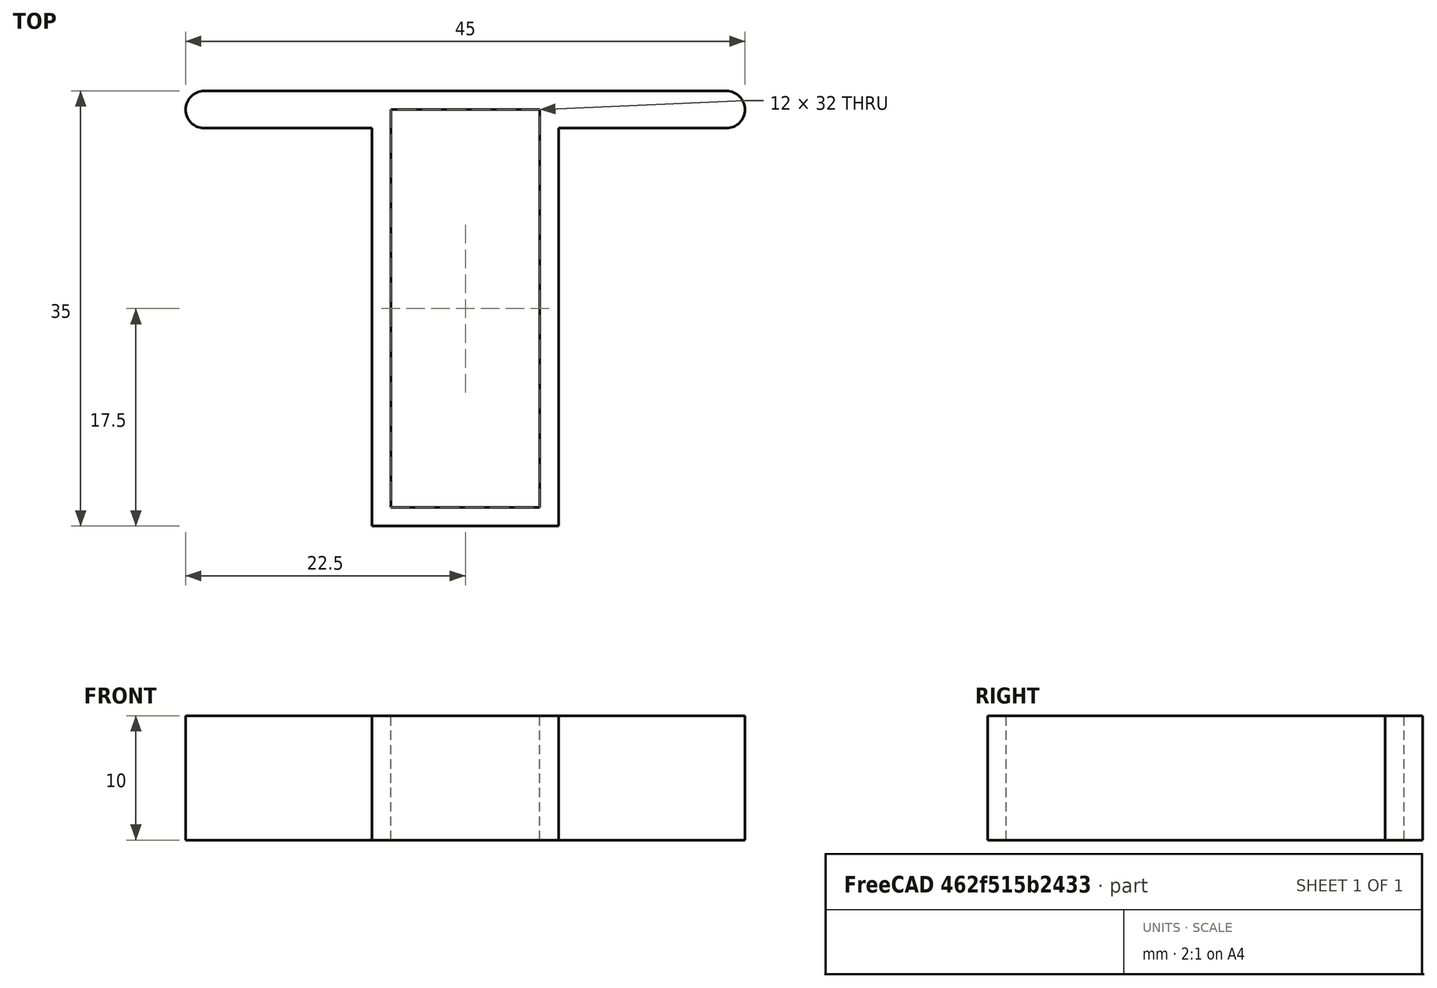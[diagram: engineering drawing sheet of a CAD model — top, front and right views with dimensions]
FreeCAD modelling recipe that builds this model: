
FCSTD DOCUMENT  (FreeCAD 0.18R16117 (Git))
Label: Perfil_R_5853
License: All rights reserved
LicenseURL: http://en.wikipedia.org/wiki/All_rights_reserved
objects: Spreadsheet::Sheet×1, Sketcher::SketchObject×1, PartDesign::Pad×1, PartDesign::Body×1
note: 4 computed .brp shape members not serialized (recipe doc carries the construction recipe); baked Part::Feature solids carry a one-line shape summary decoded from their .brp

FEATURE [Spreadsheet::Sheet] Spreadsheet  label="Tabla"
  cells = B1=Serie; C1=Serie_A; D1=Serie_B; E1=Serie_C; A2=Espesor; B2(Espesor_serie_A)=1.5; C2=1.5; D2=2; E2=2; A3=Alto; B3(Alto_serie_A)=35; C3=35; D3=50; E3=50; A4=Ancho; B4(Ancho_serie_A)=30; C4=30; D4=35; E4=60; A5=Ala; B5(Ala_serie_A)=15; C5=15; D5=15; E5=20
FEATURE [Sketcher::SketchObject] Sketch
  MapMode = 5
  Support = -> [XY_Plane]
  expr: Constraints[46] = Tabla.Ancho_serie_A + Tabla.Ala_serie_A - 2 * Tabla.Espesor_serie_A
  expr: Constraints[43] = Tabla.Alto_serie_A - Tabla.Espesor_serie_A
  expr: Constraints[45] = Tabla.Espesor_serie_A
  expr: Constraints[15] = Tabla.Ancho_serie_A - Tabla.Ala_serie_A
  expr: Constraints[42] = Tabla.Espesor_serie_A
  expr: Constraints[40] = Tabla.Espesor_serie_A
  expr: Constraints[26] = Tabla.Alto_serie_A
  expr: Constraints[38] = Tabla.Alto_serie_A - 2 * Tabla.Espesor_serie_A
  expr: Constraints[25] = Tabla.Ancho_serie_A + Tabla.Ala_serie_A
  expr: Constraints[37] = Tabla.Ancho_serie_A - Tabla.Ala_serie_A - 2 * Tabla.Espesor_serie_A
  expr: Constraints[39] = Tabla.Espesor_serie_A
  sketch-geometry (16):
    g0: LineSegment StartX=15 StartY=0 StartZ=0 EndX=15 EndY=32 EndZ=0
    g1: LineSegment StartX=15 StartY=32 StartZ=0 EndX=1.5 EndY=32 EndZ=0
    g2: LineSegment StartX=1.49999 StartY=35 StartZ=0 EndX=43.5 EndY=35 EndZ=0
    g3: LineSegment StartX=43.5 StartY=32 StartZ=0 EndX=30 EndY=32 EndZ=0
    g4: LineSegment StartX=30 StartY=32 StartZ=0 EndX=30 EndY=0 EndZ=0
    g5: LineSegment StartX=30 StartY=0 StartZ=0 EndX=15 EndY=0 EndZ=0
    g6: ArcOfCircle CenterX=43.5 CenterY=33.5 CenterZ=0 NormalX=0 NormalY=0 NormalZ=1 AngleXU=0 Radius=1.5 StartAngle=4.71239 EndAngle=7.85398
    g7: ArcOfCircle CenterX=1.5 CenterY=33.5 CenterZ=0 NormalX=0 NormalY=0 NormalZ=1 AngleXU=0 Radius=1.5 StartAngle=1.5708 EndAngle=4.71239
    g8: LineSegment [constr] StartX=0 StartY=0 StartZ=0 EndX=45 EndY=0 EndZ=0
    g9: LineSegment [constr] StartX=45 StartY=0 StartZ=0 EndX=45 EndY=35 EndZ=0
    g10: LineSegment [constr] StartX=45 StartY=35 StartZ=0 EndX=0 EndY=35 EndZ=0
    g11: LineSegment [constr] StartX=0 StartY=35 StartZ=0 EndX=0 EndY=0 EndZ=0
    g12: LineSegment StartX=16.5 StartY=33.5 StartZ=0 EndX=28.5 EndY=33.5 EndZ=0
    g13: LineSegment StartX=28.5 StartY=33.5 StartZ=0 EndX=28.5 EndY=1.5 EndZ=0
    g14: LineSegment StartX=28.5 StartY=1.5 StartZ=0 EndX=16.5 EndY=1.5 EndZ=0
    g15: LineSegment StartX=16.5 StartY=1.5 StartZ=0 EndX=16.5 EndY=33.5 EndZ=0
  constraints (47):
    c: PointOnObject(g0,g-1)
    c: Vertical(g0)
    c: Coincident(g0,g1)
    c: Horizontal(g1)
    c: Horizontal(g2)
    c: Coincident(g3,g4)
    c: PointOnObject(g4,g-1)
    c: Vertical(g4)
    c: Coincident(g4,g5)
    c: Coincident(g5,g0)
    c: Equal(g3,g1)
    c: Horizontal(g3)
    c: Coincident(g6,g2)
    c: Equal(g6,g7)
    c: Coincident(g7,g2)
    c: DistanceX(g5,g5) = 15
    c: Coincident(g8,g9)
    c: Coincident(g9,g10)
    c: Coincident(g10,g11)
    c: Coincident(g11,g8)
    c: Horizontal(g8)
    c: Horizontal(g10)
    c: Vertical(g9)
    c: Vertical(g11)
    c: Coincident(g8,g-1)
    c: DistanceX(g10,g10) = 45
    c: DistanceY(g9,g9) = 35
    c: Equal(g0,g4)
    c: PointOnObject(g2,g10)
    c: Coincident(g12,g13)
    c: Coincident(g13,g14)
    c: Coincident(g14,g15)
    c: Coincident(g15,g12)
    c: Horizontal(g12)
    c: Horizontal(g14)
    c: Vertical(g13)
    c: Vertical(g15)
    c: DistanceX(g14,g14) = 12
    c: DistanceY(g13,g13) = 32
    c: DistanceY(g0,g14) = 1.5
    c: DistanceX(g0,g14) = 1.5
    c: Tangent(g3,g6) = 1.5708
    c: Radius(g7) = 1.5
    c: DistanceY(g-1,g7) = 33.5
    c: Tangent(g7,g1) = 1.5708
    c: DistanceX(g10,g7) = 1.5
    c: DistanceX(g7,g6) = 42
FEATURE [PartDesign::Pad] Pad
  Length = 10
  Length2 = 100
  Profile = -> Sketch
  Refine = true
  Type = 0
FEATURE [PartDesign::Body] Body
  Group = -> [Sketch,Pad]
  Origin = -> Origin
  Tip = -> Pad
